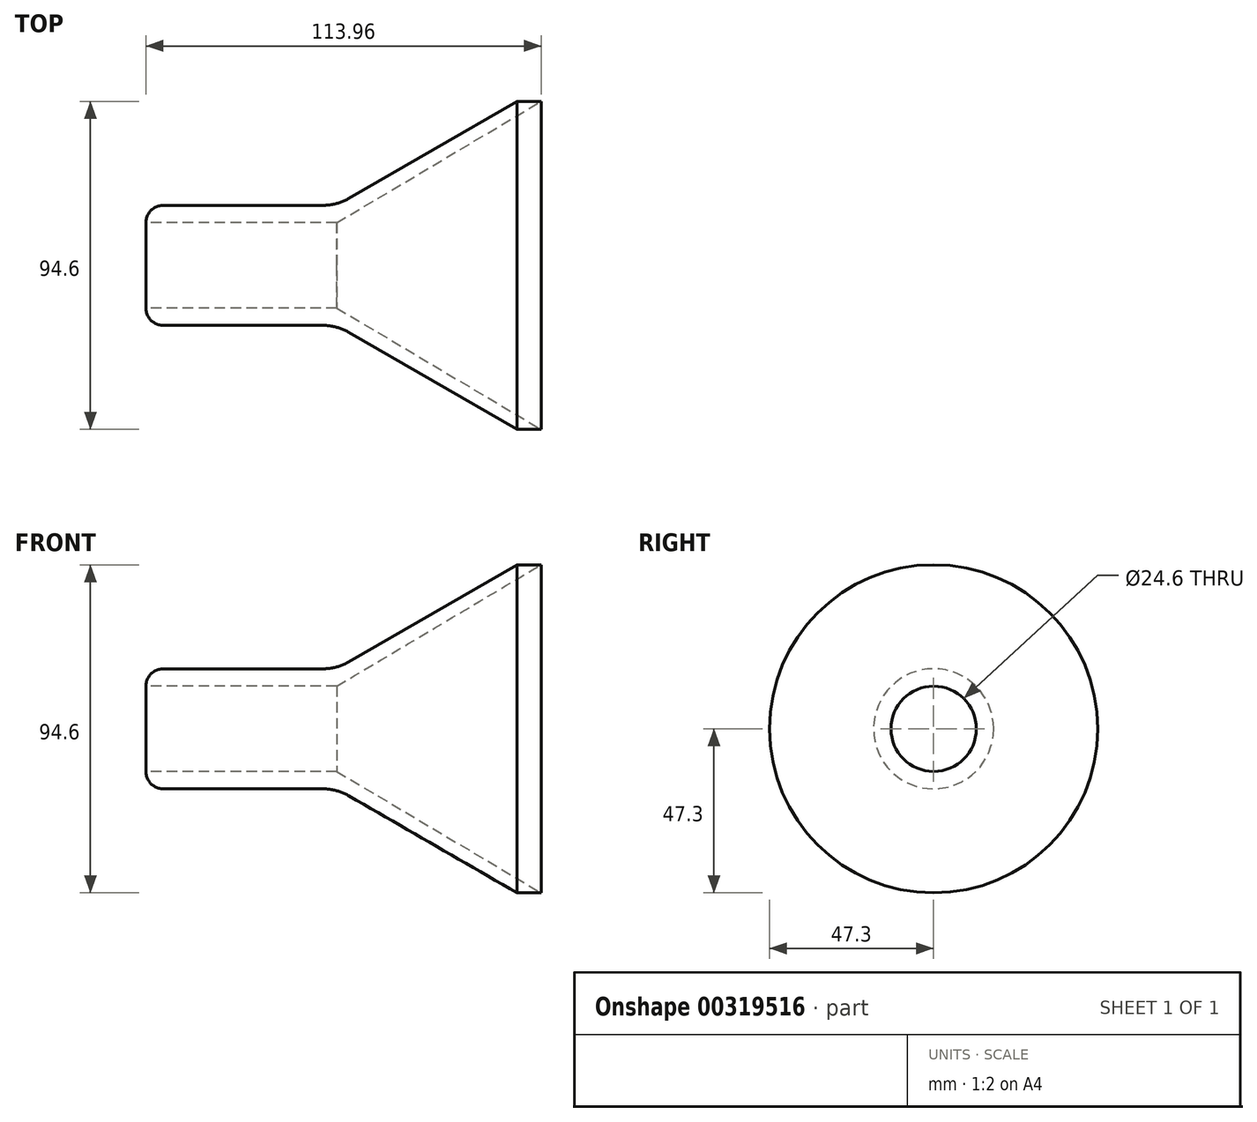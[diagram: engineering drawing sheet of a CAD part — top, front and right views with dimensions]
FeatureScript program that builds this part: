
annotation { "Feature Type Name" : "Feature", "Feature Type Description" : "" }
export const myFeature = defineFeature(function(context is Context, id is Id, definition is map)
    precondition{}
    {
        {
            var Q0;
            Q0=qCreatedBy(makeId("Front.planeOp"),FACE);
            var sketch = newSketch(context, id + "F0", { "sketchPlane" : qUnion([Q0])});
            skLineSegment(sketch, "E0", {"start": v(0, 0) * mm, "end": v(38.4, 0) * mm, "construction": true});
            skLineSegment(sketch, "E1", {"start": v(0, 17.3) * mm, "end": v(55, 17.3) * mm});
            skLineSegment(sketch, "E2", {"start": v(55, 17.3) * mm, "end": v(106.96, 47.3) * mm});
            skLineSegment(sketch, "E3", {"start": v(0, 12.3) * mm, "end": v(0, 17.3) * mm});
            skLineSegment(sketch, "E4", {"start": v(106.96, 47.3) * mm, "end": v(113.96, 47.3) * mm});
            skLineSegment(sketch, "E5", {"start": v(0, 12.3) * mm, "end": v(55, 12.3) * mm});
            skLineSegment(sketch, "E6", {"start": v(55, 12.3) * mm, "end": v(113.96, 47.3) * mm});
            skSolve(sketch);
        }
        {
            var Q0;
            Q0=makeQuery(id+"F0.imprint","IMPRINT",FACE,{"disambiguationData":[TD([[makeQuery(id+"F0.imprint","IMPRINT",EDGE,{"derivedFrom":sQuery(id+"F0.wireOp",EDGE,"E1")}),-1.0]])]});
            var Q1;
            Q1=sQuery(id+"F0.wireOp",EDGE,"E0");
            revolve(context, id + "F1", {"entities" : qUnion([Q0]), "axis" : qUnion([Q1]), "revolveType" : RevolveType.FULL});
        }
        {
            var Q0;
            Q0=makeQuery(id+"F1.opRevolve","SWEPT_EDGE",EDGE,{"disambiguationData":[OSD([sQuery(id+"F0.wireOp",EDGE,"E1"),sQuery(id+"F0.wireOp",EDGE,"E3")])]});
            fillet(context, id + "F2", {"entities" : qUnion([Q0]), "radius" : 5 * mm, "tangentPropagation" : true, "allowEdgeOverflow" : false});
        }
        {
            var Q0;
            Q0=makeQuery(id+"F1.opRevolve","SWEPT_EDGE",EDGE,{"disambiguationData":[OSD([sQuery(id+"F0.wireOp",EDGE,"E1"),sQuery(id+"F0.wireOp",EDGE,"E2")])]});
            fillet(context, id + "F3", {"entities" : qUnion([Q0]), "radius" : 15 * mm, "tangentPropagation" : true, "allowEdgeOverflow" : false});
        }
    });
